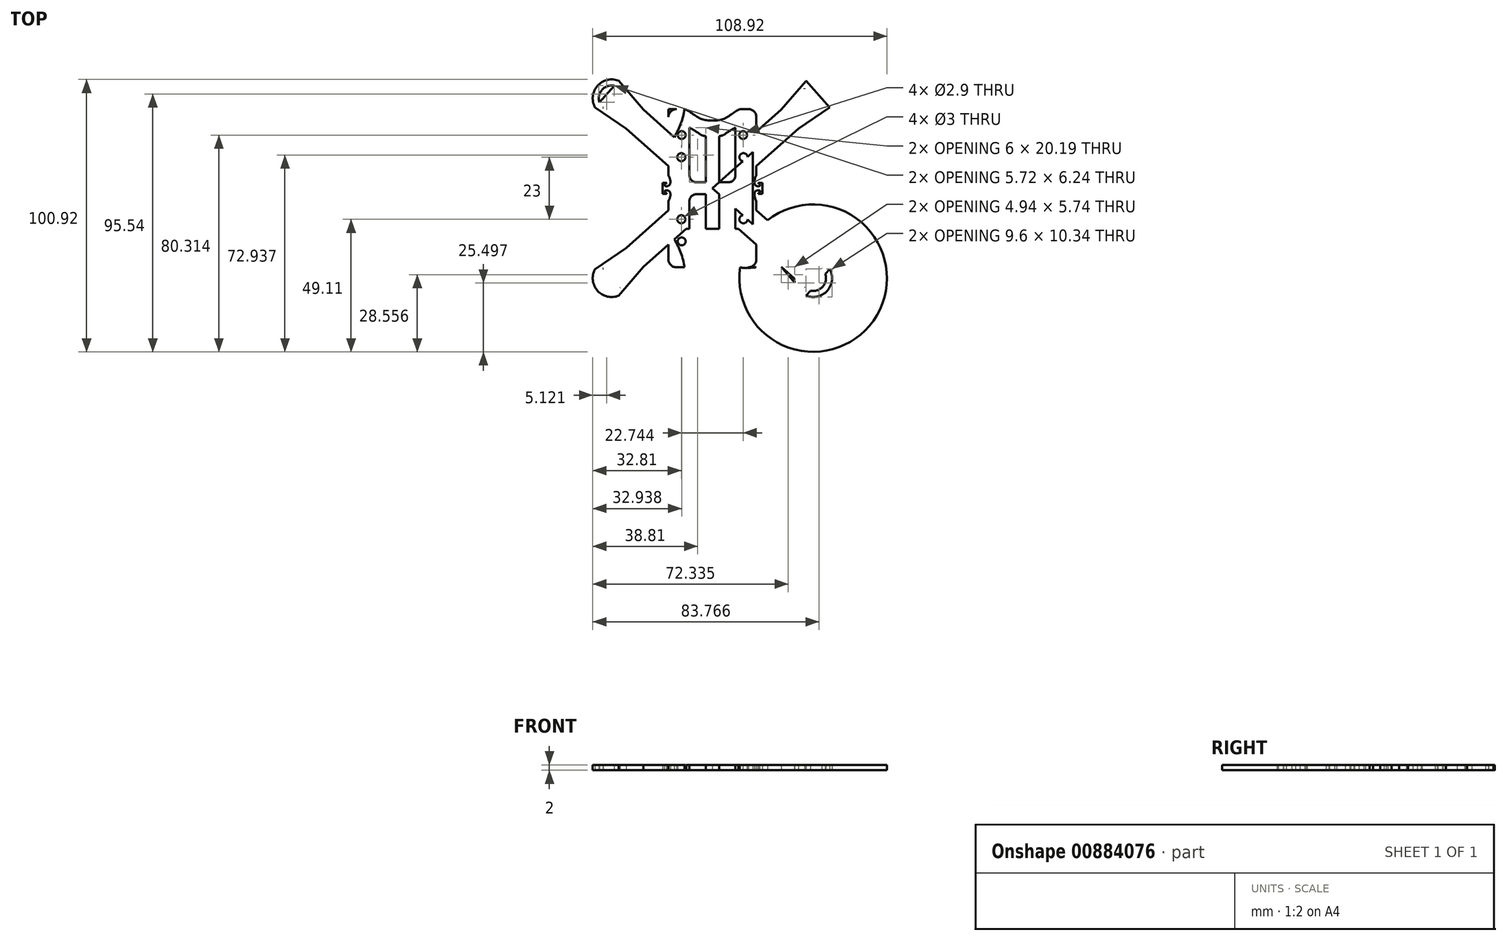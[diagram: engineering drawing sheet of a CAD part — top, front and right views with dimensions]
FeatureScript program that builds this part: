
annotation { "Feature Type Name" : "Feature", "Feature Type Description" : "" }
export const myFeature = defineFeature(function(context is Context, id is Id, definition is map)
    precondition{}
    {
        {
            var Q0;
            Q0=qCreatedBy(makeId("Top.planeOp"),FACE);
            var sketch = newSketch(context, id + "F0", { "sketchPlane" : qUnion([Q0])});
            skCircle(sketch, "E0", {"center": v(-37.3, 33.3) * mm, "radius": 27.3 * mm});
            skCircle(sketch, "E1", {"center": v(-37.3, -33.3) * mm, "radius": 27.3 * mm});
            skCircle(sketch, "E2", {"center": v(37.3, -33.3) * mm, "radius": 27.3 * mm});
            skCircle(sketch, "E3", {"center": v(37.3, 33.3) * mm, "radius": 27.3 * mm});
            skLineSegment(sketch, "E4.bottom", {"start": v(-15, 15) * mm, "end": v(15, 15) * mm});
            skLineSegment(sketch, "E4.top", {"start": v(-15, -15) * mm, "end": v(15, -15) * mm});
            skLineSegment(sketch, "E4.left", {"start": v(-15, 15) * mm, "end": v(-15, -15) * mm});
            skLineSegment(sketch, "E4.right", {"start": v(15, 15) * mm, "end": v(15, -15) * mm});
            skPoint(sketch, "E4.middle", {"position": v(0, 0) * mm});
            skLineSegment(sketch, "E5", {"start": v(37.3, -33.3) * mm, "end": v(-37.3, 33.3) * mm});
            skLineSegment(sketch, "E6", {"start": v(-37.3, -33.3) * mm, "end": v(37.3, 33.3) * mm});
            skArc(sketch, "E7", {"start": v(-30.5, -34.93) * mm, "mid": v(-32.08, -28.64) * mm, "end": v(-38.15, -26.36) * mm});
            skArc(sketch, "E8", {"start": v(43.44, 29.99) * mm, "mid": v(42.5, 37.97) * mm, "end": v(34.65, 39.76) * mm});
            skArc(sketch, "E9", {"start": v(34.65, -39.76) * mm, "mid": v(42.51, -37.95) * mm, "end": v(43.42, -29.94) * mm});
            skArc(sketch, "E10", {"start": v(-34.69, 39.8) * mm, "mid": v(-42.53, 37.97) * mm, "end": v(-43.46, 29.97) * mm});
            skCircle(sketch, "E11", {"center": v(-37.3, -33.3) * mm, "radius": 4.75 * mm});
            skCircle(sketch, "E12", {"center": v(37.3, -33.3) * mm, "radius": 4.75 * mm});
            skCircle(sketch, "E13", {"center": v(37.3, 33.3) * mm, "radius": 4.75 * mm});
            skCircle(sketch, "E14", {"center": v(-37.3, 33.3) * mm, "radius": 4.75 * mm});
            skLineSegment(sketch, "E15", {"start": v(-37.3, -33.3) * mm, "end": v(-44.5, -39.72) * mm});
            skLineSegment(sketch, "E16.MirrorCS", {"start": v(40.48, -29.78) * mm, "end": v(34.16, -36.86) * mm});
            skLineSegment(sketch, "E17", {"start": v(34.16, 36.86) * mm, "end": v(9.67, 15) * mm});
            skLineSegment(sketch, "E18", {"start": v(-40.48, 29.78) * mm, "end": v(-15, 7.02) * mm});
            skLineSegment(sketch, "E19", {"start": v(40.48, -29.78) * mm, "end": v(15, -7.02) * mm});
            skLineSegment(sketch, "E20", {"start": v(-40.48, -29.78) * mm, "end": v(-41.5, -28.64) * mm});
            skLineSegment(sketch, "E21", {"start": v(-34.16, -36.86) * mm, "end": v(-33.14, -38) * mm});
            skLineSegment(sketch, "E22", {"start": v(-43.46, -29.97) * mm, "end": v(-34.69, -39.8) * mm});
            skLineSegment(sketch, "E23", {"start": v(-43.46, -29.97) * mm, "end": v(-31.88, -22.1) * mm});
            skLineSegment(sketch, "E24.trimOffspring", {"start": v(-15, -7.02) * mm, "end": v(-40.48, -29.78) * mm});
            skLineSegment(sketch, "E25.trimOffspring", {"start": v(15, 7.02) * mm, "end": v(40.48, 29.78) * mm});
            skLineSegment(sketch, "E26.trimOffspring", {"start": v(-9.67, 15) * mm, "end": v(-34.16, 36.86) * mm});
            skLineSegment(sketch, "E27.trimOffspring", {"start": v(9.67, -15) * mm, "end": v(34.16, -36.86) * mm});
            skLineSegment(sketch, "E28.MirrorCS", {"start": v(-40.48, 29.78) * mm, "end": v(-34.16, 36.86) * mm});
            skLineSegment(sketch, "E29.MirrorCS", {"start": v(-40.48, 29.78) * mm, "end": v(-41.5, 28.64) * mm});
            skLineSegment(sketch, "E30.MirrorCS", {"start": v(-25.56, 29.18) * mm, "end": v(-34.69, 39.8) * mm});
            skLineSegment(sketch, "E31.MirrorCS", {"start": v(-43.46, 29.97) * mm, "end": v(-31.88, 22.1) * mm});
            skLineSegment(sketch, "E32.MirrorCS", {"start": v(-43.46, 29.97) * mm, "end": v(-34.69, 39.8) * mm});
            skLineSegment(sketch, "E33.MirrorCS", {"start": v(-34.16, 36.86) * mm, "end": v(-33.14, 38) * mm});
            skLineSegment(sketch, "E34.MirrorCS", {"start": v(43.46, 29.97) * mm, "end": v(31.88, 22.1) * mm});
            skLineSegment(sketch, "E35.MirrorCS", {"start": v(25.56, 29.18) * mm, "end": v(34.69, 39.8) * mm});
            skLineSegment(sketch, "E36.MirrorCS", {"start": v(40.48, 29.78) * mm, "end": v(34.16, 36.86) * mm});
            skLineSegment(sketch, "E37.MirrorCS", {"start": v(43.46, 29.97) * mm, "end": v(34.69, 39.8) * mm});
            skLineSegment(sketch, "E38.MirrorCS", {"start": v(34.16, 36.86) * mm, "end": v(33.14, 38) * mm});
            skLineSegment(sketch, "E39.MirrorCS", {"start": v(40.48, 29.78) * mm, "end": v(41.5, 28.64) * mm});
            skArc(sketch, "E40.MirrorC", {"start": v(30.5, -34.93) * mm, "mid": v(31.61, -29.23) * mm, "end": v(36.63, -26.34) * mm});
            skLineSegment(sketch, "E41.MirrorCS", {"start": v(25.56, -29.18) * mm, "end": v(34.69, -39.8) * mm});
            skLineSegment(sketch, "E42.MirrorCS", {"start": v(34.16, -36.86) * mm, "end": v(9.67, -15) * mm});
            skLineSegment(sketch, "E43.MirrorCS", {"start": v(43.46, -29.97) * mm, "end": v(34.69, -39.8) * mm});
            skLineSegment(sketch, "E44.MirrorCS", {"start": v(43.46, -29.97) * mm, "end": v(31.88, -22.1) * mm});
            skLineSegment(sketch, "E45.MirrorCS", {"start": v(40.48, -29.78) * mm, "end": v(41.5, -28.64) * mm});
            skLineSegment(sketch, "E46.MirrorCS", {"start": v(34.16, -36.86) * mm, "end": v(33.14, -38) * mm});
            skArc(sketch, "E47.trimOffspring", {"start": v(43.46, -29.97) * mm, "mid": v(42.53, -37.97) * mm, "end": v(34.69, -39.8) * mm});
            skArc(sketch, "E48.trimOffspring", {"start": v(30.53, 34.96) * mm, "mid": v(32.1, 28.66) * mm, "end": v(38.19, 26.38) * mm});
            skArc(sketch, "E49.trimOffspring", {"start": v(-38.15, 26.36) * mm, "mid": v(-32.08, 28.64) * mm, "end": v(-30.5, 34.93) * mm});
            skArc(sketch, "E50.trimOffspring", {"start": v(-43.46, -29.97) * mm, "mid": v(-42.53, -37.97) * mm, "end": v(-34.69, -39.8) * mm});
            skPoint(sketch, "E51.newPointB", {"position": v(-34.16, -36.86) * mm});
            skLineSegment(sketch, "E52.MirrorCS", {"start": v(-34.16, -36.86) * mm, "end": v(-9.67, -15) * mm});
            skLineSegment(sketch, "E53.MirrorCS", {"start": v(-25.56, -29.18) * mm, "end": v(-34.69, -39.8) * mm});
            skPoint(sketch, "E54.middle", {"position": v(0, 22.82) * mm});
            skLineSegment(sketch, "E55.bottom", {"start": v(-16.29, 29.3) * mm, "end": v(-10.3, 29.3) * mm});
            skLineSegment(sketch, "E55.top", {"start": v(-13.29, -29.3) * mm, "end": v(-10.3, -29.3) * mm});
            skLineSegment(sketch, "E55.left", {"start": v(-16.29, 29.3) * mm, "end": v(-16.29, 4.83) * mm});
            skFitSpline(sketch, "E56", {"points": [v(16.29, 29.3) * mm, v(10.3, 29.3) * mm, v(4.6, 25.86) * mm, v(0, 25.1) * mm], "startDerivative": vector(-19.72, 0) * mm, "endDerivative": vector(-14.92, -0.06) * mm});
            skFitSpline(sketch, "E57.MirrorCS", {"points": [v(-16.29, 29.3) * mm, v(-10.3, 29.3) * mm, v(-4.6, 25.86) * mm, v(0, 25.1) * mm], "startDerivative": vector(19.72, 0) * mm, "endDerivative": vector(14.92, -0.06) * mm});
            skFitSpline(sketch, "E58.MirrorCS", {"points": [v(16.29, -29.3) * mm, v(10.3, -29.3) * mm, v(4.6, -25.86) * mm, v(0, -25.1) * mm], "startDerivative": vector(-19.72, 0) * mm, "endDerivative": vector(-14.92, 0.06) * mm});
            skFitSpline(sketch, "E59.MirrorCS", {"points": [v(-16.29, -29.3) * mm, v(-10.3, -29.3) * mm, v(-4.6, -25.86) * mm, v(0, -25.1) * mm], "startDerivative": vector(19.72, 0) * mm, "endDerivative": vector(14.92, 0.06) * mm});
            skLineSegment(sketch, "E60.trimOffspring", {"start": v(10.3, 29.3) * mm, "end": v(16.29, 29.3) * mm});
            skLineSegment(sketch, "E61.trimOffspring", {"start": v(10.3, -29.3) * mm, "end": v(16.29, -29.3) * mm});
            skArc(sketch, "E62.filletArc", {"start": v(-16.29, -26.3) * mm, "mid": v(-15.41, -28.43) * mm, "end": v(-13.29, -29.3) * mm});
            skArc(sketch, "E63.MirrorCS", {"start": v(16.29, -26.3) * mm, "mid": v(15.41, -28.43) * mm, "end": v(13.29, -29.3) * mm});
            skArc(sketch, "E64.MirrorCS", {"start": v(16.29, 26.3) * mm, "mid": v(15.41, 28.43) * mm, "end": v(13.29, 29.3) * mm});
            skArc(sketch, "E65.MirrorCS", {"start": v(-16.29, 26.3) * mm, "mid": v(-15.41, 28.43) * mm, "end": v(-13.29, 29.3) * mm});
            skCircle(sketch, "E66", {"center": v(-11.37, 19.7) * mm, "radius": 1.45 * mm});
            skCircle(sketch, "E67", {"center": v(11.5, 11.5) * mm, "radius": 1.5 * mm});
            skCircle(sketch, "E68.MirrorC", {"center": v(-11.5, 11.5) * mm, "radius": 1.5 * mm});
            skCircle(sketch, "E69.MirrorC", {"center": v(11.5, -11.5) * mm, "radius": 1.5 * mm});
            skCircle(sketch, "E70.MirrorC", {"center": v(-11.5, -11.5) * mm, "radius": 1.5 * mm});
            skFitSpline(sketch, "E71", {"points": [v(-16.29, 4.83) * mm, v(-15.6, 1.81) * mm, v(-17.1, 0.75) * mm], "startDerivative": vector(3.54, -6.71) * mm, "endDerivative": vector(-7.62, -0.35) * mm});
            skLineSegment(sketch, "E72", {"start": v(-18.05, 2.04) * mm, "end": v(-18.5, 2.04) * mm});
            skLineSegment(sketch, "E73", {"start": v(-18.5, 2.04) * mm, "end": v(-18.5, 0) * mm});
            skLineSegment(sketch, "E74.MirrorCS", {"start": v(-18.5, -2.04) * mm, "end": v(-18.5, 0) * mm});
            skLineSegment(sketch, "E75.MirrorCS", {"start": v(-18.05, -2.04) * mm, "end": v(-18.5, -2.04) * mm});
            skFitSpline(sketch, "E76.MirrorCS", {"points": [v(-16.29, -4.83) * mm, v(-15.6, -1.81) * mm, v(-17.1, -0.75) * mm], "startDerivative": vector(3.54, 6.71) * mm, "endDerivative": vector(-7.62, 0.35) * mm});
            skLineSegment(sketch, "E77", {"start": v(-18.05, 2.04) * mm, "end": v(-16.95, 2.04) * mm});
            skFitSpline(sketch, "E78", {"points": [v(-16.95, 2.04) * mm, v(-17.58, 1.4) * mm, v(-17.1, 0.75) * mm], "startDerivative": vector(0.5, -1.03) * mm, "endDerivative": vector(3.51, -0.24) * mm});
            skFitSpline(sketch, "E79.MirrorCS", {"points": [v(-16.95, -2.04) * mm, v(-17.58, -1.4) * mm, v(-17.1, -0.75) * mm], "startDerivative": vector(0.5, 1.03) * mm, "endDerivative": vector(3.51, 0.24) * mm});
            skLineSegment(sketch, "E80.MirrorCS", {"start": v(-18.05, -2.04) * mm, "end": v(-16.95, -2.04) * mm});
            skPoint(sketch, "E81.orphan", {"position": v(-18.05, -2.04) * mm});
            skLineSegment(sketch, "E82.trimOffspring", {"start": v(-16.29, -4.83) * mm, "end": v(-16.29, -26.3) * mm});
            skFitSpline(sketch, "E83.MirrorCS", {"points": [v(16.29, 4.83) * mm, v(15.6, 1.81) * mm, v(17.1, 0.75) * mm], "startDerivative": vector(-3.54, -6.71) * mm, "endDerivative": vector(7.62, -0.35) * mm});
            skFitSpline(sketch, "E84.MirrorCS", {"points": [v(16.29, -4.83) * mm, v(15.6, -1.81) * mm, v(17.1, -0.75) * mm], "startDerivative": vector(-3.54, 6.71) * mm, "endDerivative": vector(7.62, 0.35) * mm});
            skFitSpline(sketch, "E85.MirrorCS", {"points": [v(16.95, -2.04) * mm, v(17.58, -1.4) * mm, v(17.1, -0.75) * mm], "startDerivative": vector(-0.5, 1.03) * mm, "endDerivative": vector(-3.51, 0.24) * mm});
            skFitSpline(sketch, "E86.MirrorCS", {"points": [v(16.95, 2.04) * mm, v(17.58, 1.4) * mm, v(17.1, 0.75) * mm], "startDerivative": vector(-0.5, -1.03) * mm, "endDerivative": vector(-3.51, -0.24) * mm});
            skLineSegment(sketch, "E87.MirrorCS", {"start": v(18.05, 2.04) * mm, "end": v(16.95, 2.04) * mm});
            skLineSegment(sketch, "E88.MirrorCS", {"start": v(18.05, 2.04) * mm, "end": v(18.5, 2.04) * mm});
            skLineSegment(sketch, "E89.MirrorCS", {"start": v(18.05, -2.04) * mm, "end": v(16.95, -2.04) * mm});
            skLineSegment(sketch, "E90.MirrorCS", {"start": v(18.05, -2.04) * mm, "end": v(18.5, -2.04) * mm});
            skLineSegment(sketch, "E91.MirrorCS", {"start": v(18.5, -2.04) * mm, "end": v(18.5, 0) * mm});
            skLineSegment(sketch, "E92.MirrorCS", {"start": v(18.5, 2.04) * mm, "end": v(18.5, 0) * mm});
            skLineSegment(sketch, "E93", {"start": v(16.29, 26.3) * mm, "end": v(16.29, 4.83) * mm});
            skLineSegment(sketch, "E94", {"start": v(16.29, -4.83) * mm, "end": v(16.29, -26.3) * mm});
            skCircle(sketch, "E95.MirrorC", {"center": v(11.37, 19.7) * mm, "radius": 1.45 * mm});
            skCircle(sketch, "E96.MirrorC", {"center": v(-11.37, -19.7) * mm, "radius": 1.45 * mm});
            skCircle(sketch, "E97.MirrorC", {"center": v(11.37, -19.7) * mm, "radius": 1.45 * mm});
            skLineSegment(sketch, "E98", {"start": v(-2.5, 19.73) * mm, "end": v(-2.5, 3.97) * mm});
            skLineSegment(sketch, "E99", {"start": v(-4.15, 2.23) * mm, "end": v(-6, 2.23) * mm});
            skLineSegment(sketch, "E100", {"start": v(-8.5, 4.73) * mm, "end": v(-8.5, 19.73) * mm});
            skPoint(sketch, "E101.visualSharp", {"position": v(-8.5, 22.23) * mm});
            skPoint(sketch, "E102.visualSharp", {"position": v(-2.5, 22.23) * mm});
            skPoint(sketch, "E103.visualSharp", {"position": v(-2.5, 2.23) * mm});
            skPoint(sketch, "E104.visualSharp", {"position": v(-8.5, 2.23) * mm});
            skArc(sketch, "E104.filletArc", {"start": v(-8.5, 4.73) * mm, "mid": v(-7.77, 2.96) * mm, "end": v(-6, 2.23) * mm});
            skLineSegment(sketch, "E105.MirrorCS", {"start": v(2.5, 19.73) * mm, "end": v(2.5, 3.97) * mm});
            skLineSegment(sketch, "E106.MirrorCS", {"start": v(8.5, 4.73) * mm, "end": v(8.5, 19.73) * mm});
            skArc(sketch, "E107.MirrorCS", {"start": v(8.5, 4.73) * mm, "mid": v(7.77, 2.96) * mm, "end": v(6, 2.23) * mm});
            skArc(sketch, "E108.MirrorCS", {"start": v(8.5, -4.73) * mm, "mid": v(7.77, -2.96) * mm, "end": v(6, -2.23) * mm});
            skArc(sketch, "E109.MirrorCS", {"start": v(-8.5, -4.73) * mm, "mid": v(-7.77, -2.96) * mm, "end": v(-6, -2.23) * mm});
            skLineSegment(sketch, "E110.MirrorCS", {"start": v(-2.5, -19.73) * mm, "end": v(-2.5, -3.97) * mm});
            skLineSegment(sketch, "E111.MirrorCS", {"start": v(-8.5, -4.73) * mm, "end": v(-8.5, -19.73) * mm});
            skLineSegment(sketch, "E112.MirrorCS", {"start": v(-4.15, -2.23) * mm, "end": v(-6, -2.23) * mm});
            skLineSegment(sketch, "E113.MirrorCS", {"start": v(4.15, 2.23) * mm, "end": v(6, 2.23) * mm});
            skLineSegment(sketch, "E114.MirrorCS", {"start": v(4.15, -2.23) * mm, "end": v(6, -2.23) * mm});
            skLineSegment(sketch, "E115.MirrorCS", {"start": v(8.5, -4.73) * mm, "end": v(8.5, -19.73) * mm});
            skLineSegment(sketch, "E116.MirrorCS", {"start": v(2.5, -19.73) * mm, "end": v(2.5, -3.97) * mm});
            skLineSegment(sketch, "E117", {"start": v(-2.5, 3.97) * mm, "end": v(-2.5, 2.23) * mm});
            skLineSegment(sketch, "E118", {"start": v(-2.5, 2.23) * mm, "end": v(-4.15, 2.23) * mm});
            skLineSegment(sketch, "E119.MirrorCS", {"start": v(-2.5, -2.23) * mm, "end": v(-4.15, -2.23) * mm});
            skLineSegment(sketch, "E120.MirrorCS", {"start": v(-2.5, -3.97) * mm, "end": v(-2.5, -2.23) * mm});
            skLineSegment(sketch, "E121.MirrorCS", {"start": v(2.5, 3.97) * mm, "end": v(2.5, 2.23) * mm});
            skLineSegment(sketch, "E122.MirrorCS", {"start": v(2.5, 2.23) * mm, "end": v(4.15, 2.23) * mm});
            skLineSegment(sketch, "E123.MirrorCS", {"start": v(2.5, -2.23) * mm, "end": v(4.15, -2.23) * mm});
            skLineSegment(sketch, "E124.MirrorCS", {"start": v(2.5, -3.97) * mm, "end": v(2.5, -2.23) * mm});
            skLineSegment(sketch, "E125", {"start": v(-2.5, -19.23) * mm, "end": v(-2.5, -19.73) * mm});
            skLineSegment(sketch, "E126", {"start": v(-8.5, -19.73) * mm, "end": v(-8.5, -22.23) * mm});
            skLineSegment(sketch, "E127.MirrorCS", {"start": v(2.5, -19.23) * mm, "end": v(2.5, -19.73) * mm});
            skLineSegment(sketch, "E128.MirrorCS", {"start": v(8, -22.23) * mm, "end": v(8.5, -22.23) * mm});
            skLineSegment(sketch, "E129.MirrorCS", {"start": v(8.5, -19.73) * mm, "end": v(8.5, -22.23) * mm});
            skLineSegment(sketch, "E130.MirrorCS", {"start": v(2.5, 19.23) * mm, "end": v(2.5, 19.73) * mm});
            skLineSegment(sketch, "E131.MirrorCS", {"start": v(8, 22.23) * mm, "end": v(8.5, 22.23) * mm});
            skLineSegment(sketch, "E132.MirrorCS", {"start": v(8.5, 19.73) * mm, "end": v(8.5, 22.23) * mm});
            skLineSegment(sketch, "E133.MirrorCS", {"start": v(-2.5, 19.23) * mm, "end": v(-2.5, 19.73) * mm});
            skLineSegment(sketch, "E134.MirrorCS", {"start": v(-8, 22.23) * mm, "end": v(-8.5, 22.23) * mm});
            skLineSegment(sketch, "E135.MirrorCS", {"start": v(-8.5, 19.73) * mm, "end": v(-8.5, 22.23) * mm});
            skPoint(sketch, "E136.end.orphan", {"position": v(-2.5, -25.23) * mm});
            skPoint(sketch, "E137.end.orphan", {"position": v(-8.5, -28.42) * mm});
            skLineSegment(sketch, "E138", {"start": v(-8.5, -22.23) * mm, "end": v(-8.5, -22.42) * mm});
            skPoint(sketch, "E139", {"position": v(-4.6, -20.06) * mm});
            skPoint(sketch, "E140", {"position": v(-2.5, -19.23) * mm});
            skPoint(sketch, "E141", {"position": v(-8.5, -22.42) * mm});
            skFitSpline(sketch, "E142", {"points": [v(-2.5, -19.23) * mm, v(-4.6, -20.06) * mm, v(-8.5, -22.42) * mm], "startDerivative": vector(-9.86, -2.36) * mm, "endDerivative": vector(-7.93, -3.79) * mm});
            skFitSpline(sketch, "E143.MirrorCS", {"points": [v(2.5, -19.23) * mm, v(4.6, -20.06) * mm, v(8.5, -22.42) * mm], "startDerivative": vector(9.86, -2.36) * mm, "endDerivative": vector(7.93, -3.79) * mm});
            skLineSegment(sketch, "E144.MirrorCS", {"start": v(8.5, -22.23) * mm, "end": v(8.5, -22.42) * mm});
            skFitSpline(sketch, "E145.MirrorCS", {"points": [v(2.5, 19.23) * mm, v(4.6, 20.06) * mm, v(8.5, 22.42) * mm], "startDerivative": vector(9.86, 2.36) * mm, "endDerivative": vector(7.93, 3.79) * mm});
            skLineSegment(sketch, "E146.MirrorCS", {"start": v(8.5, 22.23) * mm, "end": v(8.5, 22.42) * mm});
            skFitSpline(sketch, "E147.MirrorCS", {"points": [v(-2.5, 19.23) * mm, v(-4.6, 20.06) * mm, v(-8.5, 22.42) * mm], "startDerivative": vector(-9.86, 2.36) * mm, "endDerivative": vector(-7.93, 3.79) * mm});
            skLineSegment(sketch, "E148.MirrorCS", {"start": v(-8.5, 22.23) * mm, "end": v(-8.5, 22.42) * mm});
            skLineSegment(sketch, "E149", {"start": v(-40.48, -29.78) * mm, "end": v(-34.16, -36.86) * mm});
            skSolve(sketch);
        }
        {
            var Q0;
            {var subQ0=sQuery(id+"F0.wireOp",EDGE,"E117");Q0=makeQuery(id+"F0.imprint","IMPRINT",FACE,{"disambiguationData":[TD([[makeQuery(id+"F0.imprint","IMPRINT",EDGE,{"derivedFrom":subQ0}),1.0]])]});}
            var Q1;
            Q1=makeQuery(id+"F0.imprint","IMPRINT",FACE,{"disambiguationData":[TD([[makeQuery(id+"F0.imprint","IMPRINT",EDGE,{"derivedFrom":sQuery(id+"F0.wireOp",EDGE,"E99")}),1.0]])]});
            var Q2;
            Q2=makeQuery(id+"F0.imprint","IMPRINT",FACE,{"disambiguationData":[TD([[makeQuery(id+"F0.imprint","IMPRINT",EDGE,{"derivedFrom":sQuery(id+"F0.wireOp",EDGE,"E66")}),-1.0]])]});
            var Q3;
            {var subQ0=sQuery(id+"F0.wireOp",EDGE,"E65.MirrorCS");Q3=makeQuery(id+"F0.imprint","IMPRINT",FACE,{"disambiguationData":[TD([[makeQuery(id+"F0.imprint","IMPRINT",EDGE,{"derivedFrom":subQ0}),-1.0]])]});}
            var Q4;
            {var subQ0=sQuery(id+"F0.wireOp",EDGE,"E4.left");var subQ1=sQuery(id+"F0.wireOp",EDGE,"E4.bottom");var subQ2=makeQuery(id+"F0.imprint","INTERSECT",VERTEX,{"derivedFrom":[subQ1,subQ0]});Q4=makeQuery(id+"F0.imprint","IMPRINT",FACE,{"disambiguationData":[TD([[makeQuery(id+"F0.imprint","IMPRINT",EDGE,{"disambiguationData":[TD([[subQ2,-1.0]])],"derivedFrom":subQ1}),-1.0]])]});}
            var Q5;
            {var subQ3=sQuery(id+"F0.wireOp",EDGE,"E55.left");var subQ9=sQuery(id+"F0.wireOp",EDGE,"E0");var subQ10=makeQuery(id+"F0.imprint","INTERSECT",VERTEX,{"derivedFrom":[subQ9,subQ3]});Q5=makeQuery(id+"F0.imprint","IMPRINT",FACE,{"disambiguationData":[TD([[makeQuery(id+"F0.imprint","IMPRINT",EDGE,{"disambiguationData":[TD([[subQ10,-1.0]])],"derivedFrom":subQ9}),-1.0]])]});}
            var Q6;
            {var subQ20=sQuery(id+"F0.wireOp",EDGE,"E107.MirrorCS");Q6=makeQuery(id+"F0.imprint","IMPRINT",FACE,{"disambiguationData":[TD([[makeQuery(id+"F0.imprint","IMPRINT",EDGE,{"derivedFrom":subQ20}),1.0]])]});}
            var Q7;
            {var subQ5=sQuery(id+"F0.wireOp",EDGE,"E4.bottom");var subQ10=makeQuery(id+"F0.imprint","INTERSECT",VERTEX,{"derivedFrom":[subQ5,sQuery(id+"F0.wireOp",EDGE,"E17")]});Q7=makeQuery(id+"F0.imprint","IMPRINT",FACE,{"disambiguationData":[TD([[makeQuery(id+"F0.imprint","IMPRINT",EDGE,{"disambiguationData":[TD([[subQ10,1.0]])],"derivedFrom":subQ5}),-1.0]])]});}
            var Q8;
            {var subQ0=sQuery(id+"F0.wireOp",EDGE,"E64.MirrorCS");Q8=makeQuery(id+"F0.imprint","IMPRINT",FACE,{"disambiguationData":[TD([[makeQuery(id+"F0.imprint","IMPRINT",EDGE,{"derivedFrom":subQ0}),1.0]])]});}
            var Q9;
            {var subQ2=sQuery(id+"F0.wireOp",EDGE,"E93");var subQ8=sQuery(id+"F0.wireOp",EDGE,"E3");var subQ9=makeQuery(id+"F0.imprint","INTERSECT",VERTEX,{"derivedFrom":[subQ8,subQ2]});Q9=makeQuery(id+"F0.imprint","IMPRINT",FACE,{"disambiguationData":[TD([[makeQuery(id+"F0.imprint","IMPRINT",EDGE,{"disambiguationData":[TD([[subQ9,-1.0]])],"derivedFrom":subQ8}),1.0]])]});}
            var Q10;
            {var subQ0=sQuery(id+"F0.wireOp",EDGE,"E25.trimOffspring");var subQ4=sQuery(id+"F0.wireOp",EDGE,"E3");var subQ5=makeQuery(id+"F0.imprint","INTERSECT",VERTEX,{"derivedFrom":[subQ4,subQ0]});Q10=makeQuery(id+"F0.imprint","IMPRINT",FACE,{"disambiguationData":[TD([[makeQuery(id+"F0.imprint","IMPRINT",EDGE,{"disambiguationData":[TD([[subQ5,1.0]])],"derivedFrom":subQ4}),1.0]])]});}
            var Q11;
            {var subQ2=sQuery(id+"F0.wireOp",EDGE,"E36.MirrorCS");Q11=makeQuery(id+"F0.imprint","IMPRINT",FACE,{"disambiguationData":[TD([[makeQuery(id+"F0.imprint","IMPRINT",EDGE,{"derivedFrom":subQ2}),1.0]])]});}
            var Q12;
            {var subQ0=sQuery(id+"F0.wireOp",EDGE,"E13");var subQ1=sQuery(id+"F0.wireOp",EDGE,"E6");var subQ2=makeQuery(id+"F0.imprint","INTERSECT",VERTEX,{"derivedFrom":[subQ1,subQ0]});Q12=makeQuery(id+"F0.imprint","IMPRINT",FACE,{"disambiguationData":[TD([[makeQuery(id+"F0.imprint","IMPRINT",EDGE,{"disambiguationData":[TD([[subQ2,1.0]])],"derivedFrom":subQ1}),1.0]])]});}
            var Q13;
            {var subQ0=sQuery(id+"F0.wireOp",EDGE,"E38.MirrorCS");Q13=makeQuery(id+"F0.imprint","IMPRINT",FACE,{"disambiguationData":[TD([[makeQuery(id+"F0.imprint","IMPRINT",EDGE,{"derivedFrom":subQ0}),1.0]])]});}
            var Q14;
            {var subQ7=sQuery(id+"F0.wireOp",EDGE,"E38.MirrorCS");Q14=makeQuery(id+"F0.imprint","IMPRINT",FACE,{"disambiguationData":[TD([[makeQuery(id+"F0.imprint","IMPRINT",EDGE,{"derivedFrom":subQ7}),-1.0]])]});}
            var Q15;
            {var subQ0=sQuery(id+"F0.wireOp",EDGE,"E37.MirrorCS");var subQ1=sQuery(id+"F0.wireOp",EDGE,"E13");var subQ2=makeQuery(id+"F0.imprint","INTERSECT",VERTEX,{"disambiguationData":[OD(0.0)],"derivedFrom":[subQ1,subQ0]});Q15=makeQuery(id+"F0.imprint","IMPRINT",FACE,{"disambiguationData":[TD([[makeQuery(id+"F0.imprint","IMPRINT",EDGE,{"disambiguationData":[TD([[subQ2,1.0]])],"derivedFrom":subQ1}),1.0]])]});}
            var Q16;
            {var subQ0=sQuery(id+"F0.wireOp",EDGE,"E16.MirrorCS");Q16=makeQuery(id+"F0.imprint","IMPRINT",FACE,{"disambiguationData":[TD([[makeQuery(id+"F0.imprint","IMPRINT",EDGE,{"derivedFrom":subQ0}),-1.0]])]});}
            var Q17;
            {var subQ5=sQuery(id+"F0.wireOp",EDGE,"E2");var subQ8=sQuery(id+"F0.wireOp",EDGE,"E5");var subQ10=makeQuery(id+"F0.imprint","INTERSECT",VERTEX,{"derivedFrom":[subQ5,subQ8]});Q17=makeQuery(id+"F0.imprint","IMPRINT",FACE,{"disambiguationData":[TD([[makeQuery(id+"F0.imprint","IMPRINT",EDGE,{"disambiguationData":[TD([[subQ10,-1.0]])],"derivedFrom":subQ5}),1.0]])]});}
            var Q18;
            {var subQ1=sQuery(id+"F0.wireOp",EDGE,"E19");var subQ4=sQuery(id+"F0.wireOp",EDGE,"E2");var subQ5=makeQuery(id+"F0.imprint","INTERSECT",VERTEX,{"derivedFrom":[subQ4,subQ1]});Q18=makeQuery(id+"F0.imprint","IMPRINT",FACE,{"disambiguationData":[TD([[makeQuery(id+"F0.imprint","IMPRINT",EDGE,{"disambiguationData":[TD([[subQ5,-1.0]])],"derivedFrom":subQ4}),1.0]])]});}
            var Q19;
            {var subQ0=sQuery(id+"F0.wireOp",EDGE,"E36.MirrorCS");Q19=makeQuery(id+"F0.imprint","IMPRINT",FACE,{"disambiguationData":[TD([[makeQuery(id+"F0.imprint","IMPRINT",EDGE,{"derivedFrom":subQ0}),-1.0]])]});}
            var Q20;
            {var subQ0=sQuery(id+"F0.wireOp",EDGE,"E12");var subQ1=sQuery(id+"F0.wireOp",EDGE,"E5");var subQ2=makeQuery(id+"F0.imprint","INTERSECT",VERTEX,{"derivedFrom":[subQ1,subQ0]});Q20=makeQuery(id+"F0.imprint","IMPRINT",FACE,{"disambiguationData":[TD([[makeQuery(id+"F0.imprint","IMPRINT",EDGE,{"disambiguationData":[TD([[subQ2,-1.0]])],"derivedFrom":subQ1}),1.0]])]});}
            var Q21;
            {var subQ0=sQuery(id+"F0.wireOp",EDGE,"E12");var subQ1=sQuery(id+"F0.wireOp",EDGE,"E5");var subQ2=makeQuery(id+"F0.imprint","INTERSECT",VERTEX,{"derivedFrom":[subQ1,subQ0]});Q21=makeQuery(id+"F0.imprint","IMPRINT",FACE,{"disambiguationData":[TD([[makeQuery(id+"F0.imprint","IMPRINT",EDGE,{"disambiguationData":[TD([[subQ2,-1.0]])],"derivedFrom":subQ1}),-1.0]])]});}
            var Q22;
            {var subQ4=sQuery(id+"F0.wireOp",EDGE,"E45.MirrorCS");Q22=makeQuery(id+"F0.imprint","IMPRINT",FACE,{"disambiguationData":[TD([[makeQuery(id+"F0.imprint","IMPRINT",EDGE,{"derivedFrom":subQ4}),1.0]])]});}
            var Q23;
            {var subQ5=sQuery(id+"F0.wireOp",EDGE,"E17");var subQ8=sQuery(id+"F0.wireOp",EDGE,"E3");var subQ9=makeQuery(id+"F0.imprint","INTERSECT",VERTEX,{"derivedFrom":[subQ8,subQ5]});Q23=makeQuery(id+"F0.imprint","IMPRINT",FACE,{"disambiguationData":[TD([[makeQuery(id+"F0.imprint","IMPRINT",EDGE,{"disambiguationData":[TD([[subQ9,-1.0]])],"derivedFrom":subQ8}),-1.0]])]});}
            var Q24;
            {var subQ0=sQuery(id+"F0.wireOp",EDGE,"E17");var subQ1=sQuery(id+"F0.wireOp",EDGE,"E3");var subQ2=makeQuery(id+"F0.imprint","INTERSECT",VERTEX,{"derivedFrom":[subQ1,subQ0]});Q24=makeQuery(id+"F0.imprint","IMPRINT",FACE,{"disambiguationData":[TD([[makeQuery(id+"F0.imprint","IMPRINT",EDGE,{"disambiguationData":[TD([[subQ2,-1.0]])],"derivedFrom":subQ1}),1.0]])]});}
            var Q25;
            Q25=makeQuery(id+"F0.imprint","IMPRINT",FACE,{"disambiguationData":[TD([[makeQuery(id+"F0.imprint","IMPRINT",EDGE,{"derivedFrom":sQuery(id+"F0.wireOp",EDGE,"E96.MirrorC")}),1.0]])]});
            var Q26;
            {var subQ0=sQuery(id+"F0.wireOp",EDGE,"E120.MirrorCS");Q26=makeQuery(id+"F0.imprint","IMPRINT",FACE,{"disambiguationData":[TD([[makeQuery(id+"F0.imprint","IMPRINT",EDGE,{"derivedFrom":subQ0}),-1.0]])]});}
            var Q27;
            {var subQ0=sQuery(id+"F0.wireOp",EDGE,"E4.left");var subQ1=sQuery(id+"F0.wireOp",EDGE,"E4.top");var subQ2=makeQuery(id+"F0.imprint","INTERSECT",VERTEX,{"derivedFrom":[subQ1,subQ0]});Q27=makeQuery(id+"F0.imprint","IMPRINT",FACE,{"disambiguationData":[TD([[makeQuery(id+"F0.imprint","IMPRINT",EDGE,{"disambiguationData":[TD([[subQ2,-1.0]])],"derivedFrom":subQ1}),1.0]])]});}
            var Q28;
            {var subQ0=sQuery(id+"F0.wireOp",EDGE,"E55.top");Q28=makeQuery(id+"F0.imprint","IMPRINT",FACE,{"disambiguationData":[TD([[makeQuery(id+"F0.imprint","IMPRINT",EDGE,{"derivedFrom":subQ0}),1.0]])]});}
            var Q29;
            {var subQ0=sQuery(id+"F0.wireOp",EDGE,"E52.MirrorCS");var subQ1=sQuery(id+"F0.wireOp",EDGE,"E1");var subQ2=makeQuery(id+"F0.imprint","INTERSECT",VERTEX,{"derivedFrom":[subQ1,subQ0]});Q29=makeQuery(id+"F0.imprint","IMPRINT",FACE,{"disambiguationData":[TD([[makeQuery(id+"F0.imprint","IMPRINT",EDGE,{"disambiguationData":[TD([[subQ2,-1.0]])],"derivedFrom":subQ1}),1.0]])]});}
            var Q30;
            {var subQ0=sQuery(id+"F0.wireOp",EDGE,"E24.trimOffspring");var subQ1=sQuery(id+"F0.wireOp",EDGE,"E1");var subQ2=makeQuery(id+"F0.imprint","INTERSECT",VERTEX,{"derivedFrom":[subQ1,subQ0]});Q30=makeQuery(id+"F0.imprint","IMPRINT",FACE,{"disambiguationData":[TD([[makeQuery(id+"F0.imprint","IMPRINT",EDGE,{"disambiguationData":[TD([[subQ2,1.0]])],"derivedFrom":subQ1}),-1.0]])]});}
            var Q31;
            {var subQ7=sQuery(id+"F0.wireOp",EDGE,"E94");var subQ9=sQuery(id+"F0.wireOp",EDGE,"E2");var subQ10=makeQuery(id+"F0.imprint","INTERSECT",VERTEX,{"derivedFrom":[subQ9,subQ7]});Q31=makeQuery(id+"F0.imprint","IMPRINT",FACE,{"disambiguationData":[TD([[makeQuery(id+"F0.imprint","IMPRINT",EDGE,{"disambiguationData":[TD([[subQ10,-1.0]])],"derivedFrom":subQ9}),-1.0]])]});}
            var Q32;
            {var subQ0=sQuery(id+"F0.wireOp",EDGE,"E19");var subQ1=sQuery(id+"F0.wireOp",EDGE,"E4.right");var subQ2=makeQuery(id+"F0.imprint","INTERSECT",VERTEX,{"derivedFrom":[subQ1,subQ0]});Q32=makeQuery(id+"F0.imprint","IMPRINT",FACE,{"disambiguationData":[TD([[makeQuery(id+"F0.imprint","IMPRINT",EDGE,{"disambiguationData":[TD([[subQ2,-1.0]])],"derivedFrom":subQ1}),1.0]])]});}
            var Q33;
            {var subQ10=sQuery(id+"F0.wireOp",EDGE,"E83.MirrorCS");Q33=makeQuery(id+"F0.imprint","IMPRINT",FACE,{"disambiguationData":[TD([[makeQuery(id+"F0.imprint","IMPRINT",EDGE,{"derivedFrom":subQ10}),-1.0]])]});}
            var Q34;
            {var subQ0=sQuery(id+"F0.wireOp",EDGE,"E25.trimOffspring");var subQ1=sQuery(id+"F0.wireOp",EDGE,"E4.right");var subQ2=makeQuery(id+"F0.imprint","INTERSECT",VERTEX,{"derivedFrom":[subQ1,subQ0]});Q34=makeQuery(id+"F0.imprint","IMPRINT",FACE,{"disambiguationData":[TD([[makeQuery(id+"F0.imprint","IMPRINT",EDGE,{"disambiguationData":[TD([[subQ2,1.0]])],"derivedFrom":subQ1}),1.0]])]});}
            var Q35;
            {var subQ0=sQuery(id+"F0.wireOp",EDGE,"E55.left");var subQ1=sQuery(id+"F0.wireOp",EDGE,"E0");var subQ2=makeQuery(id+"F0.imprint","INTERSECT",VERTEX,{"derivedFrom":[subQ1,subQ0]});Q35=makeQuery(id+"F0.imprint","IMPRINT",FACE,{"disambiguationData":[TD([[makeQuery(id+"F0.imprint","IMPRINT",EDGE,{"disambiguationData":[TD([[subQ2,-1.0]])],"derivedFrom":subQ1}),1.0]])]});}
            var Q36;
            {var subQ0=sQuery(id+"F0.wireOp",EDGE,"E18");var subQ1=sQuery(id+"F0.wireOp",EDGE,"E4.left");var subQ2=makeQuery(id+"F0.imprint","INTERSECT",VERTEX,{"derivedFrom":[subQ1,subQ0]});Q36=makeQuery(id+"F0.imprint","IMPRINT",FACE,{"disambiguationData":[TD([[makeQuery(id+"F0.imprint","IMPRINT",EDGE,{"disambiguationData":[TD([[subQ2,1.0]])],"derivedFrom":subQ1}),-1.0]])]});}
            var Q37;
            {var subQ0=sQuery(id+"F0.wireOp",EDGE,"E71");Q37=makeQuery(id+"F0.imprint","IMPRINT",FACE,{"disambiguationData":[TD([[makeQuery(id+"F0.imprint","IMPRINT",EDGE,{"derivedFrom":subQ0}),1.0]])]});}
            var Q38;
            {var subQ0=sQuery(id+"F0.wireOp",EDGE,"E18");var subQ6=sQuery(id+"F0.wireOp",EDGE,"E0");var subQ7=makeQuery(id+"F0.imprint","INTERSECT",VERTEX,{"derivedFrom":[subQ6,subQ0]});Q38=makeQuery(id+"F0.imprint","IMPRINT",FACE,{"disambiguationData":[TD([[makeQuery(id+"F0.imprint","IMPRINT",EDGE,{"disambiguationData":[TD([[subQ7,-1.0]])],"derivedFrom":subQ6}),1.0]])]});}
            var Q39;
            {var subQ0=sQuery(id+"F0.wireOp",EDGE,"E14");var subQ1=sQuery(id+"F0.wireOp",EDGE,"E5");var subQ2=makeQuery(id+"F0.imprint","INTERSECT",VERTEX,{"derivedFrom":[subQ1,subQ0]});Q39=makeQuery(id+"F0.imprint","IMPRINT",FACE,{"disambiguationData":[TD([[makeQuery(id+"F0.imprint","IMPRINT",EDGE,{"disambiguationData":[TD([[subQ2,1.0]])],"derivedFrom":subQ1}),-1.0]])]});}
            var Q40;
            {var subQ0=sQuery(id+"F0.wireOp",EDGE,"E14");var subQ1=sQuery(id+"F0.wireOp",EDGE,"E5");var subQ2=makeQuery(id+"F0.imprint","INTERSECT",VERTEX,{"derivedFrom":[subQ1,subQ0]});Q40=makeQuery(id+"F0.imprint","IMPRINT",FACE,{"disambiguationData":[TD([[makeQuery(id+"F0.imprint","IMPRINT",EDGE,{"disambiguationData":[TD([[subQ2,1.0]])],"derivedFrom":subQ1}),1.0]])]});}
            var Q41;
            {var subQ4=sQuery(id+"F0.wireOp",EDGE,"E28.MirrorCS");Q41=makeQuery(id+"F0.imprint","IMPRINT",FACE,{"disambiguationData":[TD([[makeQuery(id+"F0.imprint","IMPRINT",EDGE,{"derivedFrom":subQ4}),-1.0]])]});}
            var Q42;
            {var subQ0=sQuery(id+"F0.wireOp",EDGE,"E33.MirrorCS");Q42=makeQuery(id+"F0.imprint","IMPRINT",FACE,{"disambiguationData":[TD([[makeQuery(id+"F0.imprint","IMPRINT",EDGE,{"derivedFrom":subQ0}),-1.0]])]});}
            var Q43;
            {var subQ0=sQuery(id+"F0.wireOp",EDGE,"E33.MirrorCS");Q43=makeQuery(id+"F0.imprint","IMPRINT",FACE,{"disambiguationData":[TD([[makeQuery(id+"F0.imprint","IMPRINT",EDGE,{"derivedFrom":subQ0}),1.0]])]});}
            var Q44;
            {var subQ0=sQuery(id+"F0.wireOp",EDGE,"E10");Q44=makeQuery(id+"F0.imprint","IMPRINT",FACE,{"disambiguationData":[TD([[makeQuery(id+"F0.imprint","IMPRINT",EDGE,{"derivedFrom":subQ0}),1.0]])]});}
            var Q45;
            {var subQ0=sQuery(id+"F0.wireOp",EDGE,"E32.MirrorCS");var subQ1=sQuery(id+"F0.wireOp",EDGE,"E14");var subQ2=makeQuery(id+"F0.imprint","INTERSECT",VERTEX,{"disambiguationData":[OD(0.0)],"derivedFrom":[subQ1,subQ0]});Q45=makeQuery(id+"F0.imprint","IMPRINT",FACE,{"disambiguationData":[TD([[makeQuery(id+"F0.imprint","IMPRINT",EDGE,{"disambiguationData":[TD([[subQ2,-1.0]])],"derivedFrom":subQ1}),1.0]])]});}
            var Q46;
            {var subQ0=sQuery(id+"F0.wireOp",EDGE,"E19");var subQ1=sQuery(id+"F0.wireOp",EDGE,"E2");var subQ2=makeQuery(id+"F0.imprint","INTERSECT",VERTEX,{"derivedFrom":[subQ1,subQ0]});Q46=makeQuery(id+"F0.imprint","IMPRINT",FACE,{"disambiguationData":[TD([[makeQuery(id+"F0.imprint","IMPRINT",EDGE,{"disambiguationData":[TD([[subQ2,-1.0]])],"derivedFrom":subQ1}),-1.0]])]});}
            var Q47;
            {var subQ0=sQuery(id+"F0.wireOp",EDGE,"E94");var subQ1=sQuery(id+"F0.wireOp",EDGE,"E2");var subQ2=makeQuery(id+"F0.imprint","INTERSECT",VERTEX,{"derivedFrom":[subQ1,subQ0]});Q47=makeQuery(id+"F0.imprint","IMPRINT",FACE,{"disambiguationData":[TD([[makeQuery(id+"F0.imprint","IMPRINT",EDGE,{"disambiguationData":[TD([[subQ2,-1.0]])],"derivedFrom":subQ1}),1.0]])]});}
            var Q48;
            {var subQ0=sQuery(id+"F0.wireOp",EDGE,"E5");var subQ1=sQuery(id+"F0.wireOp",EDGE,"E2");var subQ2=makeQuery(id+"F0.imprint","INTERSECT",VERTEX,{"derivedFrom":[subQ1,subQ0]});Q48=makeQuery(id+"F0.imprint","IMPRINT",FACE,{"disambiguationData":[TD([[makeQuery(id+"F0.imprint","IMPRINT",EDGE,{"disambiguationData":[TD([[subQ2,-1.0]])],"derivedFrom":subQ1}),-1.0]])]});}
            var Q49;
            {var subQ0=sQuery(id+"F0.wireOp",EDGE,"E28.MirrorCS");Q49=makeQuery(id+"F0.imprint","IMPRINT",FACE,{"disambiguationData":[TD([[makeQuery(id+"F0.imprint","IMPRINT",EDGE,{"derivedFrom":subQ0}),1.0]])]});}
            var Q50;
            {var subQ0=sQuery(id+"F0.wireOp",EDGE,"E29.MirrorCS");Q50=makeQuery(id+"F0.imprint","IMPRINT",FACE,{"disambiguationData":[TD([[makeQuery(id+"F0.imprint","IMPRINT",EDGE,{"derivedFrom":subQ0}),-1.0]])]});}
            var Q51;
            {var subQ0=sQuery(id+"F0.wireOp",EDGE,"E29.MirrorCS");Q51=makeQuery(id+"F0.imprint","IMPRINT",FACE,{"disambiguationData":[TD([[makeQuery(id+"F0.imprint","IMPRINT",EDGE,{"derivedFrom":subQ0}),1.0]])]});}
            var Q52;
            {var subQ0=sQuery(id+"F0.wireOp",EDGE,"E31.MirrorCS");var subQ1=sQuery(id+"F0.wireOp",EDGE,"E18");var subQ2=makeQuery(id+"F0.imprint","INTERSECT",VERTEX,{"derivedFrom":[subQ1,subQ0]});Q52=makeQuery(id+"F0.imprint","IMPRINT",FACE,{"disambiguationData":[TD([[makeQuery(id+"F0.imprint","IMPRINT",EDGE,{"disambiguationData":[TD([[subQ2,1.0]])],"derivedFrom":subQ1}),-1.0]])]});}
            var Q53;
            {var subQ0=sQuery(id+"F0.wireOp",EDGE,"E63.MirrorCS");Q53=makeQuery(id+"F0.imprint","IMPRINT",FACE,{"disambiguationData":[TD([[makeQuery(id+"F0.imprint","IMPRINT",EDGE,{"derivedFrom":subQ0}),-1.0]])]});}
            var Q54;
            {var subQ0=sQuery(id+"F0.wireOp",EDGE,"E41.MirrorCS");var subQ1=sQuery(id+"F0.wireOp",EDGE,"E40.MirrorC");var subQ2=makeQuery(id+"F0.imprint","INTERSECT",VERTEX,{"derivedFrom":[subQ1,subQ0]});Q54=makeQuery(id+"F0.imprint","IMPRINT",FACE,{"disambiguationData":[TD([[makeQuery(id+"F0.imprint","IMPRINT",EDGE,{"disambiguationData":[TD([[subQ2,-1.0]])],"derivedFrom":subQ1}),1.0]])]});}
            var Q55;
            {var subQ7=sQuery(id+"F0.wireOp",EDGE,"E46.MirrorCS");Q55=makeQuery(id+"F0.imprint","IMPRINT",FACE,{"disambiguationData":[TD([[makeQuery(id+"F0.imprint","IMPRINT",EDGE,{"derivedFrom":subQ7}),-1.0]])]});}
            var Q56;
            {var subQ7=sQuery(id+"F0.wireOp",EDGE,"E46.MirrorCS");Q56=makeQuery(id+"F0.imprint","IMPRINT",FACE,{"disambiguationData":[TD([[makeQuery(id+"F0.imprint","IMPRINT",EDGE,{"derivedFrom":subQ7}),1.0]])]});}
            var Q57;
            {var subQ0=sQuery(id+"F0.wireOp",EDGE,"E43.MirrorCS");var subQ1=sQuery(id+"F0.wireOp",EDGE,"E9");var subQ2=makeQuery(id+"F0.imprint","INTERSECT",VERTEX,{"disambiguationData":[OD(0.0)],"derivedFrom":[subQ1,subQ0]});Q57=makeQuery(id+"F0.imprint","IMPRINT",FACE,{"disambiguationData":[TD([[makeQuery(id+"F0.imprint","IMPRINT",EDGE,{"disambiguationData":[TD([[subQ2,-1.0]])],"derivedFrom":subQ1}),1.0]])]});}
            var Q58;
            {var subQ0=sQuery(id+"F0.wireOp",EDGE,"E16.MirrorCS");Q58=makeQuery(id+"F0.imprint","IMPRINT",FACE,{"disambiguationData":[TD([[makeQuery(id+"F0.imprint","IMPRINT",EDGE,{"derivedFrom":subQ0}),1.0]])]});}
            var Q59;
            {var subQ0=sQuery(id+"F0.wireOp",EDGE,"E43.MirrorCS");var subQ1=sQuery(id+"F0.wireOp",EDGE,"E12");var subQ2=makeQuery(id+"F0.imprint","INTERSECT",VERTEX,{"disambiguationData":[OD(0.0)],"derivedFrom":[subQ1,subQ0]});Q59=makeQuery(id+"F0.imprint","IMPRINT",FACE,{"disambiguationData":[TD([[makeQuery(id+"F0.imprint","IMPRINT",EDGE,{"disambiguationData":[TD([[subQ2,1.0]])],"derivedFrom":subQ1}),1.0]])]});}
            var Q60;
            {var subQ3=sQuery(id+"F0.wireOp",EDGE,"E45.MirrorCS");Q60=makeQuery(id+"F0.imprint","IMPRINT",FACE,{"disambiguationData":[TD([[makeQuery(id+"F0.imprint","IMPRINT",EDGE,{"derivedFrom":subQ3}),-1.0]])]});}
            var Q61;
            {var subQ0=sQuery(id+"F0.wireOp",EDGE,"E24.trimOffspring");var subQ2=sQuery(id+"F0.wireOp",EDGE,"E1");var subQ3=makeQuery(id+"F0.imprint","INTERSECT",VERTEX,{"derivedFrom":[subQ2,subQ0]});Q61=makeQuery(id+"F0.imprint","IMPRINT",FACE,{"disambiguationData":[TD([[makeQuery(id+"F0.imprint","IMPRINT",EDGE,{"disambiguationData":[TD([[subQ3,1.0]])],"derivedFrom":subQ2}),1.0]])]});}
            var Q62;
            {var subQ5=sQuery(id+"F0.wireOp",EDGE,"E1");var subQ8=sQuery(id+"F0.wireOp",EDGE,"E82.trimOffspring");var subQ10=makeQuery(id+"F0.imprint","INTERSECT",VERTEX,{"derivedFrom":[subQ5,subQ8]});Q62=makeQuery(id+"F0.imprint","IMPRINT",FACE,{"disambiguationData":[TD([[makeQuery(id+"F0.imprint","IMPRINT",EDGE,{"disambiguationData":[TD([[subQ10,-1.0]])],"derivedFrom":subQ5}),1.0]])]});}
            var Q63;
            {var subQ0=sQuery(id+"F0.wireOp",EDGE,"E11");var subQ1=sQuery(id+"F0.wireOp",EDGE,"E6");var subQ2=makeQuery(id+"F0.imprint","INTERSECT",VERTEX,{"derivedFrom":[subQ1,subQ0]});Q63=makeQuery(id+"F0.imprint","IMPRINT",FACE,{"disambiguationData":[TD([[makeQuery(id+"F0.imprint","IMPRINT",EDGE,{"disambiguationData":[TD([[subQ2,-1.0]])],"derivedFrom":subQ1}),-1.0]])]});}
            var Q64;
            {var subQ0=sQuery(id+"F0.wireOp",EDGE,"E11");var subQ1=sQuery(id+"F0.wireOp",EDGE,"E6");var subQ2=makeQuery(id+"F0.imprint","INTERSECT",VERTEX,{"derivedFrom":[subQ1,subQ0]});Q64=makeQuery(id+"F0.imprint","IMPRINT",FACE,{"disambiguationData":[TD([[makeQuery(id+"F0.imprint","IMPRINT",EDGE,{"disambiguationData":[TD([[subQ2,-1.0]])],"derivedFrom":subQ1}),1.0]])]});}
            var Q65;
            {var subQ0=sQuery(id+"F0.wireOp",EDGE,"Npomzuos-ScSP-avHm-3KRc-ujGKl5iepAr2");Q65=makeQuery(id+"F0.imprint","IMPRINT",FACE,{"disambiguationData":[TD([[makeQuery(id+"F0.imprint","IMPRINT",EDGE,{"derivedFrom":subQ0}),-1.0]])]});}
            var Q66;
            {var subQ5=sQuery(id+"F0.wireOp",EDGE,"E11");var subQ6=makeQuery(id+"F0.imprint","INTERSECT",VERTEX,{"derivedFrom":[subQ5,sQuery(id+"F0.wireOp",EDGE,"E52.MirrorCS")]});Q66=makeQuery(id+"F0.imprint","IMPRINT",FACE,{"disambiguationData":[TD([[makeQuery(id+"F0.imprint","IMPRINT",EDGE,{"disambiguationData":[TD([[subQ6,-1.0]])],"derivedFrom":subQ5}),1.0]])]});}
            var Q67;
            {var subQ0=sQuery(id+"F0.wireOp",EDGE,"E21");Q67=makeQuery(id+"F0.imprint","IMPRINT",FACE,{"disambiguationData":[TD([[makeQuery(id+"F0.imprint","IMPRINT",EDGE,{"derivedFrom":subQ0}),1.0]])]});}
            var Q68;
            {var subQ0=sQuery(id+"F0.wireOp",EDGE,"E53.MirrorCS");var subQ1=sQuery(id+"F0.wireOp",EDGE,"E7");var subQ2=makeQuery(id+"F0.imprint","INTERSECT",VERTEX,{"derivedFrom":[subQ1,subQ0]});Q68=makeQuery(id+"F0.imprint","IMPRINT",FACE,{"disambiguationData":[TD([[makeQuery(id+"F0.imprint","IMPRINT",EDGE,{"disambiguationData":[TD([[subQ2,-1.0]])],"derivedFrom":subQ1}),-1.0]])]});}
            var Q69;
            {var subQ0=sQuery(id+"F0.wireOp",EDGE,"E23");var subQ1=sQuery(id+"F0.wireOp",EDGE,"E7");var subQ2=makeQuery(id+"F0.imprint","INTERSECT",VERTEX,{"derivedFrom":[subQ1,subQ0]});Q69=makeQuery(id+"F0.imprint","IMPRINT",FACE,{"disambiguationData":[TD([[makeQuery(id+"F0.imprint","IMPRINT",EDGE,{"disambiguationData":[TD([[subQ2,1.0]])],"derivedFrom":subQ1}),-1.0]])]});}
            var Q70;
            {var subQ3=sQuery(id+"F0.wireOp",EDGE,"E20");Q70=makeQuery(id+"F0.imprint","IMPRINT",FACE,{"disambiguationData":[TD([[makeQuery(id+"F0.imprint","IMPRINT",EDGE,{"derivedFrom":subQ3}),-1.0]])]});}
            var Q71;
            {var subQ0=sQuery(id+"F0.wireOp",EDGE,"E20");Q71=makeQuery(id+"F0.imprint","IMPRINT",FACE,{"disambiguationData":[TD([[makeQuery(id+"F0.imprint","IMPRINT",EDGE,{"derivedFrom":subQ0}),1.0]])]});}
            var Q72;
            {var subQ0=sQuery(id+"F0.wireOp",EDGE,"GwfWPcp2-rAAy-S08y-9qAT-VXkWQvocjg7K");var subQ5=sQuery(id+"F0.wireOp",EDGE,"E15");var subQ6=makeQuery(id+"F0.imprint","INTERSECT",VERTEX,{"derivedFrom":[subQ5,subQ0]});Q72=makeQuery(id+"F0.imprint","IMPRINT",FACE,{"disambiguationData":[TD([[makeQuery(id+"F0.imprint","IMPRINT",EDGE,{"disambiguationData":[TD([[subQ6,-1.0]])],"derivedFrom":subQ5}),-1.0]])]});}
            var Q73;
            {var subQ0=sQuery(id+"F0.wireOp",EDGE,"GwfWPcp2-rAAy-S08y-9qAT-VXkWQvocjg7K");var subQ5=sQuery(id+"F0.wireOp",EDGE,"E15");var subQ6=makeQuery(id+"F0.imprint","INTERSECT",VERTEX,{"derivedFrom":[subQ5,subQ0]});Q73=makeQuery(id+"F0.imprint","IMPRINT",FACE,{"disambiguationData":[TD([[makeQuery(id+"F0.imprint","IMPRINT",EDGE,{"disambiguationData":[TD([[subQ6,-1.0]])],"derivedFrom":subQ5}),1.0]])]});}
            var Q74;
            {var subQ0=sQuery(id+"F0.wireOp",EDGE,"E21");Q74=makeQuery(id+"F0.imprint","IMPRINT",FACE,{"disambiguationData":[TD([[makeQuery(id+"F0.imprint","IMPRINT",EDGE,{"derivedFrom":subQ0}),-1.0]])]});}
            var Q75;
            {var subQ0=sQuery(id+"F0.wireOp",EDGE,"E15");var subQ1=sQuery(id+"F0.wireOp",EDGE,"E11");var subQ2=makeQuery(id+"F0.imprint","INTERSECT",VERTEX,{"derivedFrom":[subQ1,subQ0]});Q75=makeQuery(id+"F0.imprint","IMPRINT",FACE,{"disambiguationData":[TD([[makeQuery(id+"F0.imprint","IMPRINT",EDGE,{"disambiguationData":[TD([[subQ2,-1.0]])],"derivedFrom":subQ1}),-1.0]])]});}
            var Q76;
            {var subQ0=sQuery(id+"F0.wireOp",EDGE,"E22");var subQ1=sQuery(id+"F0.wireOp",EDGE,"E11");var subQ2=makeQuery(id+"F0.imprint","INTERSECT",VERTEX,{"disambiguationData":[OD(0.0)],"derivedFrom":[subQ1,subQ0]});Q76=makeQuery(id+"F0.imprint","IMPRINT",FACE,{"disambiguationData":[TD([[makeQuery(id+"F0.imprint","IMPRINT",EDGE,{"disambiguationData":[TD([[subQ2,-1.0]])],"derivedFrom":subQ1}),-1.0]])]});}
            var Q77;
            {var subQ0=sQuery(id+"F0.wireOp",EDGE,"E22");var subQ1=sQuery(id+"F0.wireOp",EDGE,"E11");var subQ2=makeQuery(id+"F0.imprint","INTERSECT",VERTEX,{"disambiguationData":[OD(0.0)],"derivedFrom":[subQ1,subQ0]});Q77=makeQuery(id+"F0.imprint","IMPRINT",FACE,{"disambiguationData":[TD([[makeQuery(id+"F0.imprint","IMPRINT",EDGE,{"disambiguationData":[TD([[subQ2,-1.0]])],"derivedFrom":subQ1}),1.0]])]});}
            var Q78;
            {var subQ0=sQuery(id+"F0.wireOp",EDGE,"E15");var subQ1=sQuery(id+"F0.wireOp",EDGE,"E11");var subQ2=makeQuery(id+"F0.imprint","INTERSECT",VERTEX,{"derivedFrom":[subQ1,subQ0]});Q78=makeQuery(id+"F0.imprint","IMPRINT",FACE,{"disambiguationData":[TD([[makeQuery(id+"F0.imprint","IMPRINT",EDGE,{"disambiguationData":[TD([[subQ2,-1.0]])],"derivedFrom":subQ1}),1.0]])]});}
            var Q79;
            {var subQ0=sQuery(id+"F0.wireOp",EDGE,"E82.trimOffspring");var subQ1=sQuery(id+"F0.wireOp",EDGE,"E1");var subQ2=makeQuery(id+"F0.imprint","INTERSECT",VERTEX,{"derivedFrom":[subQ1,subQ0]});Q79=makeQuery(id+"F0.imprint","IMPRINT",FACE,{"disambiguationData":[TD([[makeQuery(id+"F0.imprint","IMPRINT",EDGE,{"disambiguationData":[TD([[subQ2,-1.0]])],"derivedFrom":subQ1}),-1.0]])]});}
            var Q80;
            {var subQ5=sQuery(id+"F0.wireOp",EDGE,"E52.MirrorCS");var subQ8=sQuery(id+"F0.wireOp",EDGE,"E1");var subQ11=makeQuery(id+"F0.imprint","INTERSECT",VERTEX,{"derivedFrom":[subQ8,subQ5]});Q80=makeQuery(id+"F0.imprint","IMPRINT",FACE,{"disambiguationData":[TD([[makeQuery(id+"F0.imprint","IMPRINT",EDGE,{"disambiguationData":[TD([[subQ11,-1.0]])],"derivedFrom":subQ8}),-1.0]])]});}
            var Q81;
            {var subQ0=sQuery(id+"F0.wireOp",EDGE,"E24.trimOffspring");var subQ1=sQuery(id+"F0.wireOp",EDGE,"E4.left");var subQ2=makeQuery(id+"F0.imprint","INTERSECT",VERTEX,{"derivedFrom":[subQ1,subQ0]});Q81=makeQuery(id+"F0.imprint","IMPRINT",FACE,{"disambiguationData":[TD([[makeQuery(id+"F0.imprint","IMPRINT",EDGE,{"disambiguationData":[TD([[subQ2,-1.0]])],"derivedFrom":subQ1}),-1.0]])]});}
            var Q82;
            {var subQ0=sQuery(id+"F0.wireOp",EDGE,"E18");var subQ1=sQuery(id+"F0.wireOp",EDGE,"E0");var subQ2=makeQuery(id+"F0.imprint","INTERSECT",VERTEX,{"derivedFrom":[subQ1,subQ0]});Q82=makeQuery(id+"F0.imprint","IMPRINT",FACE,{"disambiguationData":[TD([[makeQuery(id+"F0.imprint","IMPRINT",EDGE,{"disambiguationData":[TD([[subQ2,-1.0]])],"derivedFrom":subQ1}),-1.0]])]});}
            var Q83;
            {var subQ5=sQuery(id+"F0.wireOp",EDGE,"E4.top");var subQ7=makeQuery(id+"F0.imprint","INTERSECT",VERTEX,{"derivedFrom":[subQ5,sQuery(id+"F0.wireOp",EDGE,"E42.MirrorCS")]});Q83=makeQuery(id+"F0.imprint","IMPRINT",FACE,{"disambiguationData":[TD([[makeQuery(id+"F0.imprint","IMPRINT",EDGE,{"disambiguationData":[TD([[subQ7,1.0]])],"derivedFrom":subQ5}),1.0]])]});}
            var Q84;
            {var subQ0=sQuery(id+"F0.wireOp",EDGE,"E13");var subQ1=sQuery(id+"F0.wireOp",EDGE,"E6");var subQ2=makeQuery(id+"F0.imprint","INTERSECT",VERTEX,{"derivedFrom":[subQ1,subQ0]});Q84=makeQuery(id+"F0.imprint","IMPRINT",FACE,{"disambiguationData":[TD([[makeQuery(id+"F0.imprint","IMPRINT",EDGE,{"disambiguationData":[TD([[subQ2,1.0]])],"derivedFrom":subQ1}),-1.0]])]});}
            var Q85;
            {var subQ0=sQuery(id+"F0.wireOp",EDGE,"E34.MirrorCS");var subQ1=sQuery(id+"F0.wireOp",EDGE,"E25.trimOffspring");var subQ2=makeQuery(id+"F0.imprint","INTERSECT",VERTEX,{"derivedFrom":[subQ1,subQ0]});Q85=makeQuery(id+"F0.imprint","IMPRINT",FACE,{"disambiguationData":[TD([[makeQuery(id+"F0.imprint","IMPRINT",EDGE,{"disambiguationData":[TD([[subQ2,-1.0]])],"derivedFrom":subQ1}),-1.0]])]});}
            var Q86;
            {var subQ0=sQuery(id+"F0.wireOp",EDGE,"E39.MirrorCS");Q86=makeQuery(id+"F0.imprint","IMPRINT",FACE,{"disambiguationData":[TD([[makeQuery(id+"F0.imprint","IMPRINT",EDGE,{"derivedFrom":subQ0}),-1.0]])]});}
            var Q87;
            {var subQ3=sQuery(id+"F0.wireOp",EDGE,"E39.MirrorCS");Q87=makeQuery(id+"F0.imprint","IMPRINT",FACE,{"disambiguationData":[TD([[makeQuery(id+"F0.imprint","IMPRINT",EDGE,{"derivedFrom":subQ3}),1.0]])]});}
            var Q88;
            {var subQ0=sQuery(id+"F0.wireOp",EDGE,"E37.MirrorCS");var subQ1=sQuery(id+"F0.wireOp",EDGE,"E8");var subQ2=makeQuery(id+"F0.imprint","INTERSECT",VERTEX,{"disambiguationData":[OD(0.0)],"derivedFrom":[subQ1,subQ0]});Q88=makeQuery(id+"F0.imprint","IMPRINT",FACE,{"disambiguationData":[TD([[makeQuery(id+"F0.imprint","IMPRINT",EDGE,{"disambiguationData":[TD([[subQ2,-1.0]])],"derivedFrom":subQ1}),1.0]])]});}
            var Q89;
            {var subQ0=sQuery(id+"F0.wireOp",EDGE,"E35.MirrorCS");var subQ1=sQuery(id+"F0.wireOp",EDGE,"E17");var subQ2=makeQuery(id+"F0.imprint","INTERSECT",VERTEX,{"derivedFrom":[subQ1,subQ0]});Q89=makeQuery(id+"F0.imprint","IMPRINT",FACE,{"disambiguationData":[TD([[makeQuery(id+"F0.imprint","IMPRINT",EDGE,{"disambiguationData":[TD([[subQ2,1.0]])],"derivedFrom":subQ1}),-1.0]])]});}
            var Q90;
            {var subQ0=sQuery(id+"F0.wireOp",EDGE,"E30.MirrorCS");var subQ1=sQuery(id+"F0.wireOp",EDGE,"E26.trimOffspring");var subQ2=makeQuery(id+"F0.imprint","INTERSECT",VERTEX,{"derivedFrom":[subQ1,subQ0]});Q90=makeQuery(id+"F0.imprint","IMPRINT",FACE,{"disambiguationData":[TD([[makeQuery(id+"F0.imprint","IMPRINT",EDGE,{"disambiguationData":[TD([[subQ2,-1.0]])],"derivedFrom":subQ1}),-1.0]])]});}
            var Q91;
            {var subQ6=sQuery(id+"F0.wireOp",EDGE,"E5");var subQ7=sQuery(id+"F0.wireOp",EDGE,"E0");var subQ8=makeQuery(id+"F0.imprint","INTERSECT",VERTEX,{"derivedFrom":[subQ7,subQ6]});Q91=makeQuery(id+"F0.imprint","IMPRINT",FACE,{"disambiguationData":[TD([[makeQuery(id+"F0.imprint","IMPRINT",EDGE,{"disambiguationData":[TD([[subQ8,-1.0]])],"derivedFrom":subQ7}),1.0]])]});}
            var Q92;
            {var subQ0=sQuery(id+"F0.wireOp",EDGE,"E5");var subQ1=sQuery(id+"F0.wireOp",EDGE,"E0");var subQ2=makeQuery(id+"F0.imprint","INTERSECT",VERTEX,{"derivedFrom":[subQ1,subQ0]});Q92=makeQuery(id+"F0.imprint","IMPRINT",FACE,{"disambiguationData":[TD([[makeQuery(id+"F0.imprint","IMPRINT",EDGE,{"disambiguationData":[TD([[subQ2,-1.0]])],"derivedFrom":subQ1}),-1.0]])]});}
            var Q93;
            {var subQ0=sQuery(id+"F0.wireOp",EDGE,"E93");var subQ1=sQuery(id+"F0.wireOp",EDGE,"E3");var subQ2=makeQuery(id+"F0.imprint","INTERSECT",VERTEX,{"derivedFrom":[subQ1,subQ0]});Q93=makeQuery(id+"F0.imprint","IMPRINT",FACE,{"disambiguationData":[TD([[makeQuery(id+"F0.imprint","IMPRINT",EDGE,{"disambiguationData":[TD([[subQ2,-1.0]])],"derivedFrom":subQ1}),-1.0]])]});}
            var Q94;
            {var subQ0=sQuery(id+"F0.wireOp",EDGE,"E25.trimOffspring");var subQ1=sQuery(id+"F0.wireOp",EDGE,"E3");var subQ2=makeQuery(id+"F0.imprint","INTERSECT",VERTEX,{"derivedFrom":[subQ1,subQ0]});Q94=makeQuery(id+"F0.imprint","IMPRINT",FACE,{"disambiguationData":[TD([[makeQuery(id+"F0.imprint","IMPRINT",EDGE,{"disambiguationData":[TD([[subQ2,1.0]])],"derivedFrom":subQ1}),-1.0]])]});}
            var Q95;
            {var subQ0=sQuery(id+"F0.wireOp",EDGE,"E15");var subQ1=sQuery(id+"F0.wireOp",EDGE,"E6");var subQ2=makeQuery(id+"F0.imprint","INTERSECT",VERTEX,{"derivedFrom":[subQ1,subQ0]});Q95=makeQuery(id+"F0.imprint","IMPRINT",FACE,{"disambiguationData":[TD([[makeQuery(id+"F0.imprint","IMPRINT",EDGE,{"disambiguationData":[TD([[subQ2,-1.0]])],"derivedFrom":subQ1}),1.0]])]});}
            var Q96;
            {var subQ0=sQuery(id+"F0.wireOp",EDGE,"E149");var subQ5=sQuery(id+"F0.wireOp",EDGE,"E15");var subQ7=makeQuery(id+"F0.imprint","INTERSECT",VERTEX,{"derivedFrom":[subQ5,subQ0]});Q96=makeQuery(id+"F0.imprint","IMPRINT",FACE,{"disambiguationData":[TD([[makeQuery(id+"F0.imprint","IMPRINT",EDGE,{"disambiguationData":[TD([[subQ7,-1.0]])],"derivedFrom":subQ5}),-1.0]])]});}
            var Q97;
            {var subQ0=sQuery(id+"F0.wireOp",EDGE,"E149");var subQ5=sQuery(id+"F0.wireOp",EDGE,"E15");var subQ6=makeQuery(id+"F0.imprint","INTERSECT",VERTEX,{"derivedFrom":[subQ5,subQ0]});Q97=makeQuery(id+"F0.imprint","IMPRINT",FACE,{"disambiguationData":[TD([[makeQuery(id+"F0.imprint","IMPRINT",EDGE,{"disambiguationData":[TD([[subQ6,-1.0]])],"derivedFrom":subQ5}),1.0]])]});}
            extrude(context, id + "F1", {"entities" : qUnion([Q0, Q1, Q2, Q3, Q4, Q5, Q6, Q7, Q8, Q9, Q10, Q11, Q12, Q13, Q14, Q15, Q16, Q17, Q18, Q19, Q20, Q21, Q22, Q23, Q24, Q25, Q26, Q27, Q28, Q29, Q30, Q31, Q32, Q33, Q34, Q35, Q36, Q37, Q38, Q39, Q40, Q41, Q42, Q43, Q44, Q45, Q46, Q47, Q48, Q49, Q50, Q51, Q52, Q53, Q54, Q55, Q56, Q57, Q58, Q59, Q60, Q61, Q62, Q63, Q64, Q65, Q66, Q67, Q68, Q69, Q70, Q71, Q72, Q73, Q74, Q75, Q76, Q77, Q78, Q79, Q80, Q81, Q82, Q83, Q84, Q85, Q86, Q87, Q88, Q89, Q90, Q91, Q92, Q93, Q94, Q95, Q96, Q97]), "depth" : 2 * mm, "offsetDistance" : 25 * mm});
        }
    });
